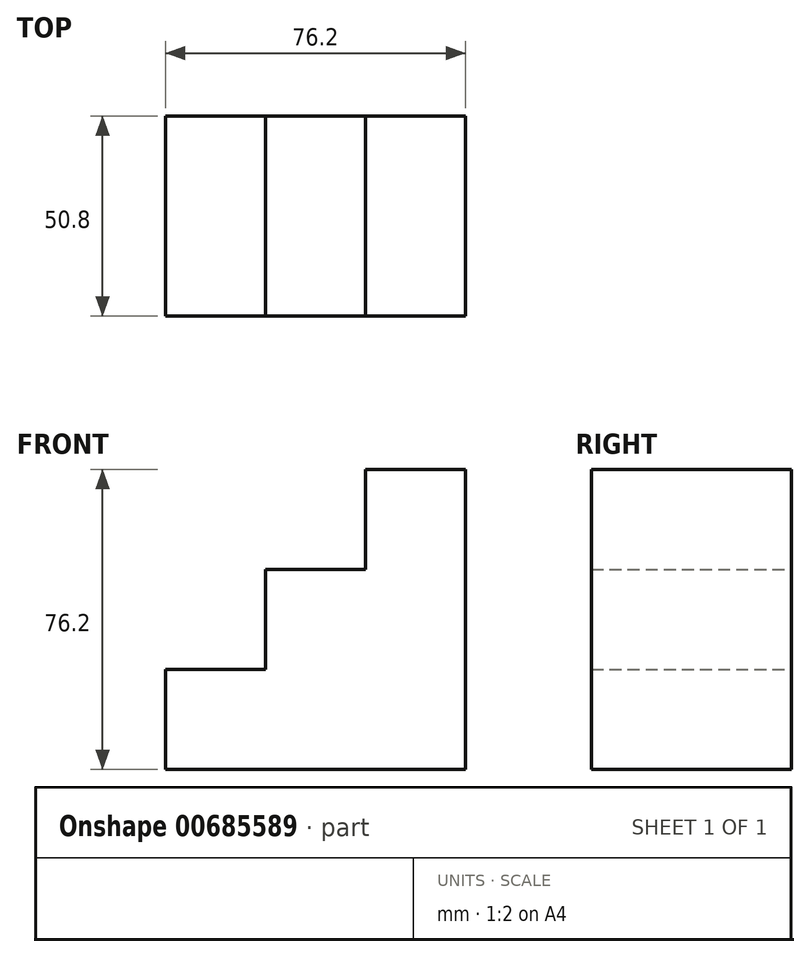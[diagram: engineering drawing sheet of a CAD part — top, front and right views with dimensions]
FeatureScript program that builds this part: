
annotation { "Feature Type Name" : "Feature", "Feature Type Description" : "" }
export const myFeature = defineFeature(function(context is Context, id is Id, definition is map)
    precondition{}
    {
        {
            var Q0;
            Q0=qCreatedBy(makeId("Front.planeOp"),FACE);
            var sketch = newSketch(context, id + "F0", { "sketchPlane" : qUnion([Q0])});
            skLineSegment(sketch, "E0", {"start": v(46.7, -13.42) * mm, "end": v(-29.5, -13.42) * mm});
            skLineSegment(sketch, "E1", {"start": v(-29.5, -13.42) * mm, "end": v(-29.5, 11.98) * mm});
            skLineSegment(sketch, "E2", {"start": v(-29.5, 11.98) * mm, "end": v(-4.1, 11.98) * mm});
            skLineSegment(sketch, "E3", {"start": v(-4.1, 11.98) * mm, "end": v(-4.1, 37.38) * mm});
            skLineSegment(sketch, "E4", {"start": v(-4.1, 37.38) * mm, "end": v(21.3, 37.38) * mm});
            skLineSegment(sketch, "E5", {"start": v(21.3, 37.38) * mm, "end": v(21.3, 62.78) * mm});
            skLineSegment(sketch, "E6", {"start": v(21.3, 62.78) * mm, "end": v(46.7, 62.78) * mm});
            skLineSegment(sketch, "E7", {"start": v(46.7, 62.78) * mm, "end": v(46.7, -13.42) * mm});
            skSolve(sketch);
        }
        {
            var Q0;
            Q0 = qSketchRegion(id + "F0", true);
            extrude(context, id + "F1", {"entities" : qUnion([Q0]), "depth" : 50.8 * mm, "offsetDistance" : 25.4 * mm});
        }
    });
